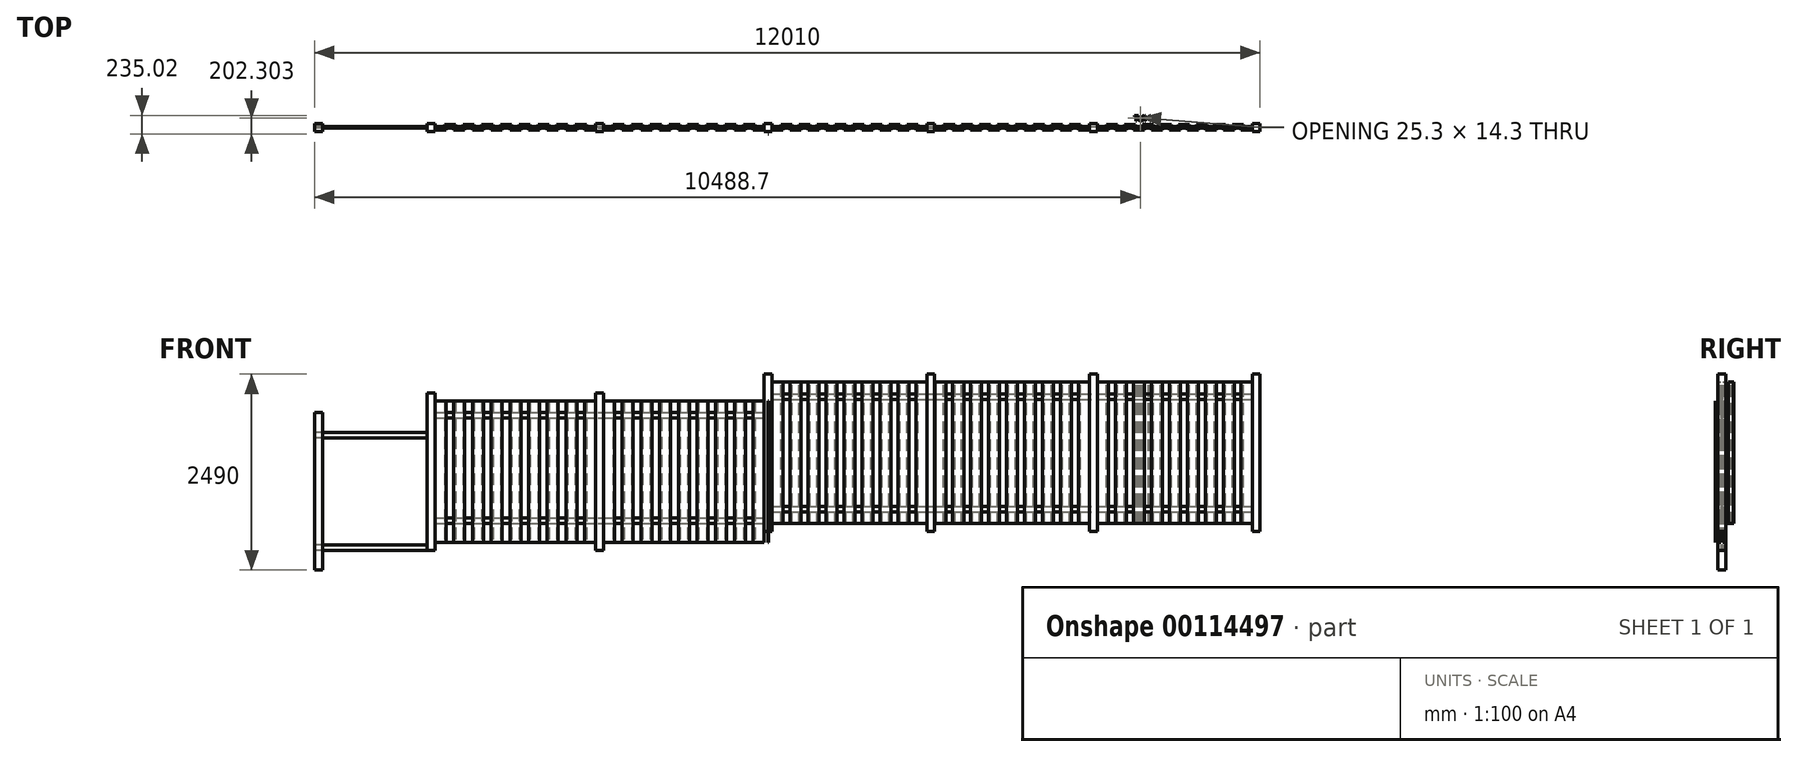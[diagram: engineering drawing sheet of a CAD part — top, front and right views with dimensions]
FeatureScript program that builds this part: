
annotation { "Feature Type Name" : "Feature", "Feature Type Description" : "" }
export const myFeature = defineFeature(function(context is Context, id is Id, definition is map)
    precondition{}
    {
        {
            var Q0;
            Q0=qCreatedBy(makeId("Top.planeOp"),FACE);
            var sketch = newSketch(context, id + "F0", { "sketchPlane" : qUnion([Q0])});
            skLineSegment(sketch, "E0.bottom", {"start": v(0, 0) * mm, "end": v(-100, 0) * mm});
            skLineSegment(sketch, "E0.top", {"start": v(0, 100) * mm, "end": v(-100, 100) * mm});
            skLineSegment(sketch, "E0.left", {"start": v(0, 0) * mm, "end": v(0, 100) * mm});
            skLineSegment(sketch, "E0.right", {"start": v(-100, 0) * mm, "end": v(-100, 100) * mm});
            skLineSegment(sketch, "E1.bottom", {"start": v(-6200, 0) * mm, "end": v(-6300, 0) * mm});
            skLineSegment(sketch, "E1.top", {"start": v(-6200, 100) * mm, "end": v(-6300, 100) * mm});
            skLineSegment(sketch, "E1.left", {"start": v(-6200, 0) * mm, "end": v(-6200, 100) * mm});
            skLineSegment(sketch, "E1.right", {"start": v(-6300, 0) * mm, "end": v(-6300, 100) * mm});
            skLineSegment(sketch, "E2.bottom", {"start": v(-10480, 0) * mm, "end": v(-10580, 0) * mm});
            skLineSegment(sketch, "E2.top", {"start": v(-10480, 100) * mm, "end": v(-10580, 100) * mm});
            skLineSegment(sketch, "E2.left", {"start": v(-10480, 0) * mm, "end": v(-10480, 100) * mm});
            skLineSegment(sketch, "E2.right", {"start": v(-10580, 0) * mm, "end": v(-10580, 100) * mm});
            skLineSegment(sketch, "E3.bottom", {"start": v(-2066.5, 0) * mm, "end": v(-2166.5, 0) * mm});
            skLineSegment(sketch, "E3.top", {"start": v(-2066.5, 100) * mm, "end": v(-2166.5, 100) * mm});
            skLineSegment(sketch, "E3.left", {"start": v(-2066.5, 0) * mm, "end": v(-2066.5, 100) * mm});
            skLineSegment(sketch, "E3.right", {"start": v(-2166.5, 0) * mm, "end": v(-2166.5, 100) * mm});
            skLineSegment(sketch, "E4.bottom", {"start": v(-4133, 0) * mm, "end": v(-4233, 0) * mm});
            skLineSegment(sketch, "E4.top", {"start": v(-4133, 100) * mm, "end": v(-4233, 100) * mm});
            skLineSegment(sketch, "E4.left", {"start": v(-4133, 0) * mm, "end": v(-4133, 100) * mm});
            skLineSegment(sketch, "E4.right", {"start": v(-4233, 0) * mm, "end": v(-4233, 100) * mm});
            skLineSegment(sketch, "E5.bottom", {"start": v(-11910, 0) * mm, "end": v(-12010, 0) * mm});
            skLineSegment(sketch, "E5.top", {"start": v(-11910, 100) * mm, "end": v(-12010, 100) * mm});
            skLineSegment(sketch, "E5.left", {"start": v(-11910, 0) * mm, "end": v(-11910, 100) * mm});
            skLineSegment(sketch, "E5.right", {"start": v(-12010, 0) * mm, "end": v(-12010, 100) * mm});
            skLineSegment(sketch, "E6.bottom", {"start": v(-8340, 0) * mm, "end": v(-8440, 0) * mm});
            skLineSegment(sketch, "E6.top", {"start": v(-8340, 100) * mm, "end": v(-8440, 100) * mm});
            skLineSegment(sketch, "E6.left", {"start": v(-8340, 0) * mm, "end": v(-8340, 100) * mm});
            skLineSegment(sketch, "E6.right", {"start": v(-8440, 0) * mm, "end": v(-8440, 100) * mm});
            skSolve(sketch);
        }
        {
            var Q0;
            Q0=makeQuery(id+"F0.imprint","IMPRINT",FACE,{"disambiguationData":[TD([[makeQuery(id+"F0.imprint","IMPRINT",EDGE,{"derivedFrom":sQuery(id+"F0.wireOp",EDGE,"E1.bottom")}),-1.0]])]});
            var Q1;
            Q1=makeQuery(id+"F0.imprint","IMPRINT",FACE,{"disambiguationData":[TD([[makeQuery(id+"F0.imprint","IMPRINT",EDGE,{"derivedFrom":sQuery(id+"F0.wireOp",EDGE,"E4.bottom")}),-1.0]])]});
            var Q2;
            Q2=makeQuery(id+"F0.imprint","IMPRINT",FACE,{"disambiguationData":[TD([[makeQuery(id+"F0.imprint","IMPRINT",EDGE,{"derivedFrom":sQuery(id+"F0.wireOp",EDGE,"E3.bottom")}),-1.0]])]});
            var Q3;
            Q3=makeQuery(id+"F0.imprint","IMPRINT",FACE,{"disambiguationData":[TD([[makeQuery(id+"F0.imprint","IMPRINT",EDGE,{"derivedFrom":sQuery(id+"F0.wireOp",EDGE,"E0.bottom")}),-1.0]])]});
            extrude(context, id + "F1", {"entities" : qUnion([Q0, Q1, Q2, Q3]), "depth" : 2000 * mm});
        }
        {
            var Q0;
            Q0=makeQuery(id+"F0.imprint","IMPRINT",FACE,{"disambiguationData":[TD([[makeQuery(id+"F0.imprint","IMPRINT",EDGE,{"derivedFrom":sQuery(id+"F0.wireOp",EDGE,"E6.bottom")}),-1.0]])]});
            var Q1;
            Q1=makeQuery(id+"F0.imprint","IMPRINT",FACE,{"disambiguationData":[TD([[makeQuery(id+"F0.imprint","IMPRINT",EDGE,{"derivedFrom":sQuery(id+"F0.wireOp",EDGE,"E2.bottom")}),-1.0]])]});
            extrude(context, id + "F2", {"entities" : qUnion([Q0, Q1]), "depth" : (2000 - 240) * mm, "hasSecondDirection" : true, "secondDirectionOppositeDirection" : true, "secondDirectionDepth" : 240 * mm});
        }
        {
            var Q0;
            Q0=makeQuery(id+"F0.imprint","IMPRINT",FACE,{"disambiguationData":[TD([[makeQuery(id+"F0.imprint","IMPRINT",EDGE,{"derivedFrom":sQuery(id+"F0.wireOp",EDGE,"E5.bottom")}),-1.0]])]});
            extrude(context, id + "F3", {"entities" : qUnion([Q0]), "depth" : (2000 - 490) * mm, "hasSecondDirection" : true, "secondDirectionOppositeDirection" : true, "secondDirectionDepth" : (240 + 250) * mm});
        }
        {
            var Q0;
            Q0=makeQuery(id+"F1.opExtrude","SWEPT_FACE",FACE,{"disambiguationData":[OSD([sQuery(id+"F0.wireOp",EDGE,"E0.left")])]});
            var sketch = newSketch(context, id + "F4", { "sketchPlane" : qUnion([Q0])});
            skLineSegment(sketch, "E7.bottom", {"start": v(39, 320) * mm, "end": v(61, 320) * mm});
            skLineSegment(sketch, "E7.top", {"start": v(39, 250) * mm, "end": v(61, 250) * mm});
            skLineSegment(sketch, "E7.left", {"start": v(39, 320) * mm, "end": v(39, 250) * mm});
            skLineSegment(sketch, "E7.right", {"start": v(61, 320) * mm, "end": v(61, 250) * mm});
            skLineSegment(sketch, "E8.bottom", {"start": v(39, 1680) * mm, "end": v(61, 1680) * mm});
            skLineSegment(sketch, "E8.top", {"start": v(39, 1750) * mm, "end": v(61, 1750) * mm});
            skLineSegment(sketch, "E8.left", {"start": v(39, 1680) * mm, "end": v(39, 1750) * mm});
            skLineSegment(sketch, "E8.right", {"start": v(61, 1680) * mm, "end": v(61, 1750) * mm});
            skSolve(sketch);
        }
        {
            var Q0;
            Q0 = qSketchRegion(id + "F4", true);
            var Q1;
            Q1=makeQuery(id+"F1.opExtrude","SWEPT_FACE",FACE,{"disambiguationData":[OSD([sQuery(id+"F0.wireOp",EDGE,"E1.left")])]});
            extrude(context, id + "F5", {"entities" : qUnion([Q0]), "endBound" : BoundingType.UP_TO_SURFACE, "oppositeDirection" : true, "endBoundEntityFace" : qUnion([Q1]), "depth" : 25 * mm, "hasSecondDirection" : true, "secondDirectionOppositeDirection" : true, "secondDirectionDepth" : 100 * mm});
        }
        {
            var Q0;
            Q0=makeQuery(id+"F1.opExtrude","SWEPT_FACE",FACE,{"disambiguationData":[OSD([sQuery(id+"F0.wireOp",EDGE,"E1.right")])]});
            var sketch = newSketch(context, id + "F6", { "sketchPlane" : qUnion([Q0])});
            skLineSegment(sketch, "E9.bottom", {"start": v(-39, 1510) * mm, "end": v(-61, 1510) * mm});
            skLineSegment(sketch, "E9.top", {"start": v(-39, 1440) * mm, "end": v(-61, 1440) * mm});
            skLineSegment(sketch, "E9.left", {"start": v(-39, 1510) * mm, "end": v(-39, 1440) * mm});
            skLineSegment(sketch, "E9.right", {"start": v(-61, 1510) * mm, "end": v(-61, 1440) * mm});
            skLineSegment(sketch, "E10.bottom", {"start": v(-39, 174.78) * mm, "end": v(-61, 174.78) * mm});
            skLineSegment(sketch, "E10.top", {"start": v(-39, 104.78) * mm, "end": v(-61, 104.78) * mm});
            skLineSegment(sketch, "E10.left", {"start": v(-39, 174.78) * mm, "end": v(-39, 104.78) * mm});
            skLineSegment(sketch, "E10.right", {"start": v(-61, 174.78) * mm, "end": v(-61, 104.78) * mm});
            skSolve(sketch);
        }
        {
            var Q0;
            Q0 = qSketchRegion(id + "F6", true);
            var Q1;
            Q1=makeQuery(id+"F2.opExtrude","SWEPT_FACE",FACE,{"disambiguationData":[OSD([sQuery(id+"F0.wireOp",EDGE,"E2.left")])]});
            extrude(context, id + "F7", {"entities" : qUnion([Q0]), "endBound" : BoundingType.UP_TO_SURFACE, "endBoundEntityFace" : qUnion([Q1]), "depth" : 25 * mm});
        }
        {
            var Q0;
            Q0=makeQuery(id+"F1.opExtrude","CAP_FACE",FACE,{"disambiguationData":[OSD([sQuery(id+"F0.wireOp",EDGE,"E3.bottom"),sQuery(id+"F0.wireOp",EDGE,"E3.top"),sQuery(id+"F0.wireOp",EDGE,"E3.left"),sQuery(id+"F0.wireOp",EDGE,"E3.right")])],"isStart":false});
            var sketch = newSketch(context, id + "F8", { "sketchPlane" : qUnion([Q0])});
            skLineSegment(sketch, "E11.bottom", {"start": v(-2066.5, 39) * mm, "end": v(-1926.5, 39) * mm});
            skLineSegment(sketch, "E11.top", {"start": v(-2066.5, 17) * mm, "end": v(-1926.5, 17) * mm});
            skLineSegment(sketch, "E11.left", {"start": v(-2066.5, 39) * mm, "end": v(-2066.5, 17) * mm});
            skLineSegment(sketch, "E11.right", {"start": v(-1926.5, 39) * mm, "end": v(-1926.5, 17) * mm});
            skLineSegment(sketch, "E12.1.0.0", {"start": v(-1838.2, 39) * mm, "end": v(-1838.2, 17) * mm});
            skLineSegment(sketch, "E12.1.0.1", {"start": v(-1838.2, 17) * mm, "end": v(-1698.2, 17) * mm});
            skLineSegment(sketch, "E12.1.0.2", {"start": v(-1838.2, 39) * mm, "end": v(-1698.2, 39) * mm});
            skLineSegment(sketch, "E12.1.0.3", {"start": v(-1698.2, 39) * mm, "end": v(-1698.2, 17) * mm});
            skLineSegment(sketch, "E12.2.0.0", {"start": v(-1609.9, 39) * mm, "end": v(-1609.9, 17) * mm});
            skLineSegment(sketch, "E12.2.0.1", {"start": v(-1609.9, 17) * mm, "end": v(-1469.9, 17) * mm});
            skLineSegment(sketch, "E12.2.0.2", {"start": v(-1609.9, 39) * mm, "end": v(-1469.9, 39) * mm});
            skLineSegment(sketch, "E12.2.0.3", {"start": v(-1469.9, 39) * mm, "end": v(-1469.9, 17) * mm});
            skLineSegment(sketch, "E12.3.0.0", {"start": v(-1381.6, 39) * mm, "end": v(-1381.6, 17) * mm});
            skLineSegment(sketch, "E12.3.0.1", {"start": v(-1381.6, 17) * mm, "end": v(-1241.6, 17) * mm});
            skLineSegment(sketch, "E12.3.0.2", {"start": v(-1381.6, 39) * mm, "end": v(-1241.6, 39) * mm});
            skLineSegment(sketch, "E12.3.0.3", {"start": v(-1241.6, 39) * mm, "end": v(-1241.6, 17) * mm});
            skLineSegment(sketch, "E12.4.0.0", {"start": v(-1153.3, 39) * mm, "end": v(-1153.3, 17) * mm});
            skLineSegment(sketch, "E12.4.0.1", {"start": v(-1153.3, 17) * mm, "end": v(-1013.3, 17) * mm});
            skLineSegment(sketch, "E12.4.0.2", {"start": v(-1153.3, 39) * mm, "end": v(-1013.3, 39) * mm});
            skLineSegment(sketch, "E12.4.0.3", {"start": v(-1013.3, 39) * mm, "end": v(-1013.3, 17) * mm});
            skLineSegment(sketch, "E12.5.0.0", {"start": v(-925, 39) * mm, "end": v(-925, 17) * mm});
            skLineSegment(sketch, "E12.5.0.1", {"start": v(-925, 17) * mm, "end": v(-785, 17) * mm});
            skLineSegment(sketch, "E12.5.0.2", {"start": v(-925, 39) * mm, "end": v(-785, 39) * mm});
            skLineSegment(sketch, "E12.5.0.3", {"start": v(-785, 39) * mm, "end": v(-785, 17) * mm});
            skLineSegment(sketch, "E12.6.0.0", {"start": v(-696.7, 39) * mm, "end": v(-696.7, 17) * mm});
            skLineSegment(sketch, "E12.6.0.1", {"start": v(-696.7, 17) * mm, "end": v(-556.7, 17) * mm});
            skLineSegment(sketch, "E12.6.0.2", {"start": v(-696.7, 39) * mm, "end": v(-556.7, 39) * mm});
            skLineSegment(sketch, "E12.6.0.3", {"start": v(-556.7, 39) * mm, "end": v(-556.7, 17) * mm});
            skLineSegment(sketch, "E12.7.0.0", {"start": v(-468.4, 39) * mm, "end": v(-468.4, 17) * mm});
            skLineSegment(sketch, "E12.7.0.1", {"start": v(-468.4, 17) * mm, "end": v(-328.4, 17) * mm});
            skLineSegment(sketch, "E12.7.0.2", {"start": v(-468.4, 39) * mm, "end": v(-328.4, 39) * mm});
            skLineSegment(sketch, "E12.7.0.3", {"start": v(-328.4, 39) * mm, "end": v(-328.4, 17) * mm});
            skLineSegment(sketch, "E12.8.0.0", {"start": v(-240.1, 39) * mm, "end": v(-240.1, 17) * mm});
            skLineSegment(sketch, "E12.8.0.1", {"start": v(-240.1, 17) * mm, "end": v(-100.1, 17) * mm});
            skLineSegment(sketch, "E12.8.0.2", {"start": v(-240.1, 39) * mm, "end": v(-100.1, 39) * mm});
            skLineSegment(sketch, "E12.8.0.3", {"start": v(-100.1, 39) * mm, "end": v(-100.1, 17) * mm});
            skLineSegment(sketch, "E12.direction1", {"start": v(-2066.5, 17) * mm, "end": v(-1838.2, 17) * mm, "construction": true});
            skLineSegment(sketch, "E13.bottom", {"start": v(-1952.35, 61) * mm, "end": v(-1812.35, 61) * mm});
            skLineSegment(sketch, "E13.top", {"start": v(-1952.35, 83) * mm, "end": v(-1812.35, 83) * mm});
            skLineSegment(sketch, "E13.left", {"start": v(-1952.35, 61) * mm, "end": v(-1952.35, 83) * mm});
            skLineSegment(sketch, "E13.right", {"start": v(-1812.35, 61) * mm, "end": v(-1812.35, 83) * mm});
            skLineSegment(sketch, "E14", {"start": v(-1882.35, -3.63) * mm, "end": v(-1882.35, 53.31) * mm, "construction": true});
            skLineSegment(sketch, "E15.1.0.0", {"start": v(-1584.05, 61) * mm, "end": v(-1584.05, 83) * mm});
            skLineSegment(sketch, "E15.1.0.1", {"start": v(-1724.05, 83) * mm, "end": v(-1584.05, 83) * mm});
            skLineSegment(sketch, "E15.1.0.2", {"start": v(-1724.05, 61) * mm, "end": v(-1724.05, 83) * mm});
            skLineSegment(sketch, "E15.1.0.3", {"start": v(-1724.05, 61) * mm, "end": v(-1584.05, 61) * mm});
            skLineSegment(sketch, "E15.2.0.0", {"start": v(-1355.75, 61) * mm, "end": v(-1355.75, 83) * mm});
            skLineSegment(sketch, "E15.2.0.1", {"start": v(-1495.75, 83) * mm, "end": v(-1355.75, 83) * mm});
            skLineSegment(sketch, "E15.2.0.2", {"start": v(-1495.75, 61) * mm, "end": v(-1495.75, 83) * mm});
            skLineSegment(sketch, "E15.2.0.3", {"start": v(-1495.75, 61) * mm, "end": v(-1355.75, 61) * mm});
            skLineSegment(sketch, "E15.3.0.0", {"start": v(-1127.45, 61) * mm, "end": v(-1127.45, 83) * mm});
            skLineSegment(sketch, "E15.3.0.1", {"start": v(-1267.45, 83) * mm, "end": v(-1127.45, 83) * mm});
            skLineSegment(sketch, "E15.3.0.2", {"start": v(-1267.45, 61) * mm, "end": v(-1267.45, 83) * mm});
            skLineSegment(sketch, "E15.3.0.3", {"start": v(-1267.45, 61) * mm, "end": v(-1127.45, 61) * mm});
            skLineSegment(sketch, "E15.4.0.0", {"start": v(-899.15, 61) * mm, "end": v(-899.15, 83) * mm});
            skLineSegment(sketch, "E15.4.0.1", {"start": v(-1039.15, 83) * mm, "end": v(-899.15, 83) * mm});
            skLineSegment(sketch, "E15.4.0.2", {"start": v(-1039.15, 61) * mm, "end": v(-1039.15, 83) * mm});
            skLineSegment(sketch, "E15.4.0.3", {"start": v(-1039.15, 61) * mm, "end": v(-899.15, 61) * mm});
            skLineSegment(sketch, "E15.5.0.0", {"start": v(-670.85, 61) * mm, "end": v(-670.85, 83) * mm});
            skLineSegment(sketch, "E15.5.0.1", {"start": v(-810.85, 83) * mm, "end": v(-670.85, 83) * mm});
            skLineSegment(sketch, "E15.5.0.2", {"start": v(-810.85, 61) * mm, "end": v(-810.85, 83) * mm});
            skLineSegment(sketch, "E15.5.0.3", {"start": v(-810.85, 61) * mm, "end": v(-670.85, 61) * mm});
            skLineSegment(sketch, "E15.6.0.0", {"start": v(-442.55, 61) * mm, "end": v(-442.55, 83) * mm});
            skLineSegment(sketch, "E15.6.0.1", {"start": v(-582.55, 83) * mm, "end": v(-442.55, 83) * mm});
            skLineSegment(sketch, "E15.6.0.2", {"start": v(-582.55, 61) * mm, "end": v(-582.55, 83) * mm});
            skLineSegment(sketch, "E15.6.0.3", {"start": v(-582.55, 61) * mm, "end": v(-442.55, 61) * mm});
            skLineSegment(sketch, "E15.7.0.0", {"start": v(-214.25, 61) * mm, "end": v(-214.25, 83) * mm});
            skLineSegment(sketch, "E15.7.0.1", {"start": v(-354.25, 83) * mm, "end": v(-214.25, 83) * mm});
            skLineSegment(sketch, "E15.7.0.2", {"start": v(-354.25, 61) * mm, "end": v(-354.25, 83) * mm});
            skLineSegment(sketch, "E15.7.0.3", {"start": v(-354.25, 61) * mm, "end": v(-214.25, 61) * mm});
            skLineSegment(sketch, "E15.direction1", {"start": v(-1952.35, 61) * mm, "end": v(-1724.05, 61) * mm, "construction": true});
            skLineSegment(sketch, "E16", {"start": v(-2116.5, 100) * mm, "end": v(-2116.5, 142.57) * mm, "construction": true});
            skLineSegment(sketch, "E17.MirrorCS", {"start": v(-2394.8, 39) * mm, "end": v(-2394.8, 17) * mm});
            skLineSegment(sketch, "E18.MirrorCS", {"start": v(-2166.5, 39) * mm, "end": v(-2166.5, 17) * mm});
            skLineSegment(sketch, "E19.MirrorCS", {"start": v(-2508.95, 61) * mm, "end": v(-2508.95, 83) * mm});
            skLineSegment(sketch, "E20.MirrorCS", {"start": v(-2280.65, 61) * mm, "end": v(-2280.65, 83) * mm});
            skLineSegment(sketch, "E21.MirrorCS", {"start": v(-2534.8, 39) * mm, "end": v(-2534.8, 17) * mm});
            skLineSegment(sketch, "E22.MirrorCS", {"start": v(-2306.5, 39) * mm, "end": v(-2306.5, 17) * mm});
            skLineSegment(sketch, "E23.MirrorCS", {"start": v(-2991.4, 39) * mm, "end": v(-2991.4, 17) * mm});
            skLineSegment(sketch, "E24.MirrorCS", {"start": v(-3333.85, 61) * mm, "end": v(-3333.85, 83) * mm});
            skLineSegment(sketch, "E25.MirrorCS", {"start": v(-3904.6, 39) * mm, "end": v(-3904.6, 17) * mm});
            skLineSegment(sketch, "E26.MirrorCS", {"start": v(-2877.25, 61) * mm, "end": v(-2877.25, 83) * mm});
            skLineSegment(sketch, "E27.MirrorCS", {"start": v(-3790.45, 61) * mm, "end": v(-3790.45, 83) * mm});
            skLineSegment(sketch, "E28.MirrorCS", {"start": v(-3764.6, 39) * mm, "end": v(-3764.6, 17) * mm});
            skLineSegment(sketch, "E29.MirrorCS", {"start": v(-3422.15, 61) * mm, "end": v(-3422.15, 83) * mm});
            skLineSegment(sketch, "E30.MirrorCS", {"start": v(-2965.55, 61) * mm, "end": v(-2965.55, 83) * mm});
            skLineSegment(sketch, "E31.MirrorCS", {"start": v(-3878.75, 61) * mm, "end": v(-3878.75, 83) * mm});
            skLineSegment(sketch, "E32.MirrorCS", {"start": v(-3308, 39) * mm, "end": v(-3308, 17) * mm});
            skLineSegment(sketch, "E33.MirrorCS", {"start": v(-3992.9, 39) * mm, "end": v(-3992.9, 17) * mm});
            skLineSegment(sketch, "E34.MirrorCS", {"start": v(-3676.3, 39) * mm, "end": v(-3676.3, 17) * mm});
            skLineSegment(sketch, "E35.MirrorCS", {"start": v(-3562.15, 61) * mm, "end": v(-3562.15, 83) * mm});
            skLineSegment(sketch, "E36.MirrorCS", {"start": v(-2648.95, 61) * mm, "end": v(-2648.95, 83) * mm});
            skLineSegment(sketch, "E37.MirrorCS", {"start": v(-3448, 39) * mm, "end": v(-3448, 17) * mm});
            skLineSegment(sketch, "E38.MirrorCS", {"start": v(-4132.9, 39) * mm, "end": v(-4132.9, 17) * mm});
            skLineSegment(sketch, "E39.MirrorCS", {"start": v(-3219.7, 39) * mm, "end": v(-3219.7, 17) * mm});
            skLineSegment(sketch, "E40.MirrorCS", {"start": v(-2623.1, 39) * mm, "end": v(-2623.1, 17) * mm});
            skLineSegment(sketch, "E41.MirrorCS", {"start": v(-3079.7, 39) * mm, "end": v(-3079.7, 17) * mm});
            skLineSegment(sketch, "E42.MirrorCS", {"start": v(-4018.75, 61) * mm, "end": v(-4018.75, 83) * mm});
            skLineSegment(sketch, "E43.MirrorCS", {"start": v(-3650.45, 61) * mm, "end": v(-3650.45, 83) * mm});
            skLineSegment(sketch, "E44.MirrorCS", {"start": v(-2737.25, 61) * mm, "end": v(-2737.25, 83) * mm});
            skLineSegment(sketch, "E45.MirrorCS", {"start": v(-2763.1, 39) * mm, "end": v(-2763.1, 17) * mm});
            skLineSegment(sketch, "E46.MirrorCS", {"start": v(-3536.3, 39) * mm, "end": v(-3536.3, 17) * mm});
            skLineSegment(sketch, "E47.MirrorCS", {"start": v(-2420.65, 61) * mm, "end": v(-2420.65, 83) * mm});
            skLineSegment(sketch, "E48.MirrorCS", {"start": v(-3193.85, 61) * mm, "end": v(-3193.85, 83) * mm});
            skLineSegment(sketch, "E49.MirrorCS", {"start": v(-3105.55, 61) * mm, "end": v(-3105.55, 83) * mm});
            skLineSegment(sketch, "E50.MirrorCS", {"start": v(-2851.4, 39) * mm, "end": v(-2851.4, 17) * mm});
            skLineSegment(sketch, "E51.MirrorCS", {"start": v(-2166.5, 17) * mm, "end": v(-2306.5, 17) * mm});
            skLineSegment(sketch, "E52.MirrorCS", {"start": v(-2280.65, 61) * mm, "end": v(-2420.65, 61) * mm});
            skLineSegment(sketch, "E53.MirrorCS", {"start": v(-2350.65, -3.63) * mm, "end": v(-2350.65, 53.31) * mm, "construction": true});
            skLineSegment(sketch, "E54.MirrorCS", {"start": v(-2394.8, 39) * mm, "end": v(-2534.8, 39) * mm});
            skLineSegment(sketch, "E55.MirrorCS", {"start": v(-2394.8, 17) * mm, "end": v(-2534.8, 17) * mm});
            skLineSegment(sketch, "E56.MirrorCS", {"start": v(-2166.5, 39) * mm, "end": v(-2306.5, 39) * mm});
            skLineSegment(sketch, "E57.MirrorCS", {"start": v(-2851.4, 39) * mm, "end": v(-2991.4, 39) * mm});
            skLineSegment(sketch, "E58.MirrorCS", {"start": v(-2851.4, 17) * mm, "end": v(-2991.4, 17) * mm});
            skLineSegment(sketch, "E59.MirrorCS", {"start": v(-2737.25, 83) * mm, "end": v(-2877.25, 83) * mm});
            skLineSegment(sketch, "E60.MirrorCS", {"start": v(-3650.45, 83) * mm, "end": v(-3790.45, 83) * mm});
            skLineSegment(sketch, "E61.MirrorCS", {"start": v(-2166.5, 17) * mm, "end": v(-2394.8, 17) * mm, "construction": true});
            skLineSegment(sketch, "E62.MirrorCS", {"start": v(-2280.65, 61) * mm, "end": v(-2508.95, 61) * mm, "construction": true});
            skLineSegment(sketch, "E63.MirrorCS", {"start": v(-3308, 39) * mm, "end": v(-3448, 39) * mm});
            skLineSegment(sketch, "E64.MirrorCS", {"start": v(-2280.65, 83) * mm, "end": v(-2420.65, 83) * mm});
            skLineSegment(sketch, "E65.MirrorCS", {"start": v(-2965.55, 61) * mm, "end": v(-3105.55, 61) * mm});
            skLineSegment(sketch, "E66.MirrorCS", {"start": v(-3878.75, 61) * mm, "end": v(-4018.75, 61) * mm});
            skLineSegment(sketch, "E67.MirrorCS", {"start": v(-3308, 17) * mm, "end": v(-3448, 17) * mm});
            skLineSegment(sketch, "E68.MirrorCS", {"start": v(-3764.6, 39) * mm, "end": v(-3904.6, 39) * mm});
            skLineSegment(sketch, "E69.MirrorCS", {"start": v(-2508.95, 61) * mm, "end": v(-2648.95, 61) * mm});
            skLineSegment(sketch, "E70.MirrorCS", {"start": v(-3422.15, 61) * mm, "end": v(-3562.15, 61) * mm});
            skLineSegment(sketch, "E71.MirrorCS", {"start": v(-3764.6, 17) * mm, "end": v(-3904.6, 17) * mm});
            skLineSegment(sketch, "E72.MirrorCS", {"start": v(-2623.1, 17) * mm, "end": v(-2763.1, 17) * mm});
            skLineSegment(sketch, "E73.MirrorCS", {"start": v(-2508.95, 83) * mm, "end": v(-2648.95, 83) * mm});
            skLineSegment(sketch, "E74.MirrorCS", {"start": v(-3536.3, 39) * mm, "end": v(-3676.3, 39) * mm});
            skLineSegment(sketch, "E75.MirrorCS", {"start": v(-3193.85, 83) * mm, "end": v(-3333.85, 83) * mm});
            skLineSegment(sketch, "E76.MirrorCS", {"start": v(-3992.9, 17) * mm, "end": v(-4132.9, 17) * mm});
            skLineSegment(sketch, "E77.MirrorCS", {"start": v(-3079.7, 17) * mm, "end": v(-3219.7, 17) * mm});
            skLineSegment(sketch, "E78.MirrorCS", {"start": v(-3650.45, 61) * mm, "end": v(-3790.45, 61) * mm});
            skLineSegment(sketch, "E79.MirrorCS", {"start": v(-2737.25, 61) * mm, "end": v(-2877.25, 61) * mm});
            skLineSegment(sketch, "E80.MirrorCS", {"start": v(-3878.75, 83) * mm, "end": v(-4018.75, 83) * mm});
            skLineSegment(sketch, "E81.MirrorCS", {"start": v(-2965.55, 83) * mm, "end": v(-3105.55, 83) * mm});
            skLineSegment(sketch, "E82.MirrorCS", {"start": v(-3422.15, 83) * mm, "end": v(-3562.15, 83) * mm});
            skLineSegment(sketch, "E83.MirrorCS", {"start": v(-2623.1, 39) * mm, "end": v(-2763.1, 39) * mm});
            skLineSegment(sketch, "E84.MirrorCS", {"start": v(-3536.3, 17) * mm, "end": v(-3676.3, 17) * mm});
            skLineSegment(sketch, "E85.MirrorCS", {"start": v(-3193.85, 61) * mm, "end": v(-3333.85, 61) * mm});
            skLineSegment(sketch, "E86.MirrorCS", {"start": v(-3992.9, 39) * mm, "end": v(-4132.9, 39) * mm});
            skLineSegment(sketch, "E87.MirrorCS", {"start": v(-3079.7, 39) * mm, "end": v(-3219.7, 39) * mm});
            skLineSegment(sketch, "E88", {"start": v(-4183, 101.05) * mm, "end": v(-4183, 169.36) * mm, "construction": true});
            skLineSegment(sketch, "E89.MirrorCS", {"start": v(-4233.1, 39) * mm, "end": v(-4233.1, 17) * mm});
            skLineSegment(sketch, "E90.MirrorCS", {"start": v(-6199.5, 39) * mm, "end": v(-6199.5, 17) * mm});
            skLineSegment(sketch, "E91.MirrorCS", {"start": v(-5286.3, 39) * mm, "end": v(-5286.3, 17) * mm});
            skLineSegment(sketch, "E92.MirrorCS", {"start": v(-4461.4, 39) * mm, "end": v(-4461.4, 17) * mm});
            skLineSegment(sketch, "E93.MirrorCS", {"start": v(-4347.25, 61) * mm, "end": v(-4347.25, 83) * mm});
            skLineSegment(sketch, "E94.MirrorCS", {"start": v(-5488.75, 61) * mm, "end": v(-5488.75, 83) * mm});
            skLineSegment(sketch, "E95.MirrorCS", {"start": v(-4575.55, 61) * mm, "end": v(-4575.55, 83) * mm});
            skLineSegment(sketch, "E96.MirrorCS", {"start": v(-5400.45, 61) * mm, "end": v(-5400.45, 83) * mm});
            skLineSegment(sketch, "E97.MirrorCS", {"start": v(-5945.35, 61) * mm, "end": v(-5945.35, 83) * mm});
            skLineSegment(sketch, "E98.MirrorCS", {"start": v(-5971.2, 39) * mm, "end": v(-5971.2, 17) * mm});
            skLineSegment(sketch, "E99.MirrorCS", {"start": v(-6199.5, 17) * mm, "end": v(-6059.5, 17) * mm});
            skLineSegment(sketch, "E100.MirrorCS", {"start": v(-5514.6, 39) * mm, "end": v(-5514.6, 17) * mm});
            skLineSegment(sketch, "E101.MirrorCS", {"start": v(-5857.05, 83) * mm, "end": v(-5717.05, 83) * mm});
            skLineSegment(sketch, "E102.MirrorCS", {"start": v(-5514.6, 39) * mm, "end": v(-5374.6, 39) * mm});
            skLineSegment(sketch, "E103.MirrorCS", {"start": v(-4829.7, 39) * mm, "end": v(-4689.7, 39) * mm});
            skLineSegment(sketch, "E104.MirrorCS", {"start": v(-5514.6, 17) * mm, "end": v(-5374.6, 17) * mm});
            skLineSegment(sketch, "E105.MirrorCS", {"start": v(-4715.55, 61) * mm, "end": v(-4715.55, 83) * mm});
            skLineSegment(sketch, "E106.MirrorCS", {"start": v(-5172.15, 83) * mm, "end": v(-5032.15, 83) * mm});
            skLineSegment(sketch, "E107.MirrorCS", {"start": v(-5628.75, 83) * mm, "end": v(-5488.75, 83) * mm});
            skLineSegment(sketch, "E108.MirrorCS", {"start": v(-4715.55, 83) * mm, "end": v(-4575.55, 83) * mm});
            skLineSegment(sketch, "E109.MirrorCS", {"start": v(-5628.75, 61) * mm, "end": v(-5628.75, 83) * mm});
            skLineSegment(sketch, "E110.MirrorCS", {"start": v(-4601.4, 39) * mm, "end": v(-4601.4, 17) * mm});
            skLineSegment(sketch, "E111.MirrorCS", {"start": v(-5602.9, 39) * mm, "end": v(-5602.9, 17) * mm});
            skLineSegment(sketch, "E112.MirrorCS", {"start": v(-5286.3, 17) * mm, "end": v(-5146.3, 17) * mm});
            skLineSegment(sketch, "E113.MirrorCS", {"start": v(-6199.5, 17) * mm, "end": v(-5971.2, 17) * mm, "construction": true});
            skLineSegment(sketch, "E114.MirrorCS", {"start": v(-4829.7, 39) * mm, "end": v(-4829.7, 17) * mm});
            skLineSegment(sketch, "E115.MirrorCS", {"start": v(-4715.55, 61) * mm, "end": v(-4575.55, 61) * mm});
            skLineSegment(sketch, "E116.MirrorCS", {"start": v(-6085.35, 61) * mm, "end": v(-5857.05, 61) * mm, "construction": true});
            skLineSegment(sketch, "E117.MirrorCS", {"start": v(-4487.25, 61) * mm, "end": v(-4487.25, 83) * mm});
            skLineSegment(sketch, "E118.MirrorCS", {"start": v(-5628.75, 61) * mm, "end": v(-5488.75, 61) * mm});
            skLineSegment(sketch, "E119.MirrorCS", {"start": v(-4487.25, 83) * mm, "end": v(-4347.25, 83) * mm});
            skLineSegment(sketch, "E120.MirrorCS", {"start": v(-6199.5, 39) * mm, "end": v(-6059.5, 39) * mm});
            skLineSegment(sketch, "E121.MirrorCS", {"start": v(-5742.9, 17) * mm, "end": v(-5602.9, 17) * mm});
            skLineSegment(sketch, "E122.MirrorCS", {"start": v(-5717.05, 61) * mm, "end": v(-5717.05, 83) * mm});
            skLineSegment(sketch, "E123.MirrorCS", {"start": v(-6085.35, 61) * mm, "end": v(-5945.35, 61) * mm});
            skLineSegment(sketch, "E124.MirrorCS", {"start": v(-4601.4, 39) * mm, "end": v(-4461.4, 39) * mm});
            skLineSegment(sketch, "E125.MirrorCS", {"start": v(-4829.7, 17) * mm, "end": v(-4689.7, 17) * mm});
            skLineSegment(sketch, "E126.MirrorCS", {"start": v(-5742.9, 39) * mm, "end": v(-5742.9, 17) * mm});
            skLineSegment(sketch, "E127.MirrorCS", {"start": v(-5032.15, 61) * mm, "end": v(-5032.15, 83) * mm});
            skLineSegment(sketch, "E128.MirrorCS", {"start": v(-6085.35, 61) * mm, "end": v(-6085.35, 83) * mm});
            skLineSegment(sketch, "E129.MirrorCS", {"start": v(-5971.2, 17) * mm, "end": v(-5831.2, 17) * mm});
            skLineSegment(sketch, "E130.MirrorCS", {"start": v(-4601.4, 17) * mm, "end": v(-4461.4, 17) * mm});
            skLineSegment(sketch, "E131.MirrorCS", {"start": v(-5286.3, 39) * mm, "end": v(-5146.3, 39) * mm});
            skLineSegment(sketch, "E132.MirrorCS", {"start": v(-5374.6, 39) * mm, "end": v(-5374.6, 17) * mm});
            skLineSegment(sketch, "E133.MirrorCS", {"start": v(-5146.3, 39) * mm, "end": v(-5146.3, 17) * mm});
            skLineSegment(sketch, "E134.MirrorCS", {"start": v(-5400.45, 83) * mm, "end": v(-5260.45, 83) * mm});
            skLineSegment(sketch, "E135.MirrorCS", {"start": v(-5260.45, 61) * mm, "end": v(-5260.45, 83) * mm});
            skLineSegment(sketch, "E136.MirrorCS", {"start": v(-6059.5, 39) * mm, "end": v(-6059.5, 17) * mm});
            skLineSegment(sketch, "E137.MirrorCS", {"start": v(-5831.2, 39) * mm, "end": v(-5831.2, 17) * mm});
            skLineSegment(sketch, "E138.MirrorCS", {"start": v(-5857.05, 61) * mm, "end": v(-5857.05, 83) * mm});
            skLineSegment(sketch, "E139.MirrorCS", {"start": v(-5172.15, 61) * mm, "end": v(-5032.15, 61) * mm});
            skLineSegment(sketch, "E140.MirrorCS", {"start": v(-5742.9, 39) * mm, "end": v(-5602.9, 39) * mm});
            skLineSegment(sketch, "E141.MirrorCS", {"start": v(-5857.05, 61) * mm, "end": v(-5717.05, 61) * mm});
            skLineSegment(sketch, "E142.MirrorCS", {"start": v(-6015.35, -3.63) * mm, "end": v(-6015.35, 53.31) * mm, "construction": true});
            skLineSegment(sketch, "E143.MirrorCS", {"start": v(-4803.85, 61) * mm, "end": v(-4803.85, 83) * mm});
            skLineSegment(sketch, "E144.MirrorCS", {"start": v(-5058, 39) * mm, "end": v(-5058, 17) * mm});
            skLineSegment(sketch, "E145.MirrorCS", {"start": v(-5172.15, 61) * mm, "end": v(-5172.15, 83) * mm});
            skLineSegment(sketch, "E146.MirrorCS", {"start": v(-4373.1, 39) * mm, "end": v(-4373.1, 17) * mm});
            skLineSegment(sketch, "E147.MirrorCS", {"start": v(-6085.35, 83) * mm, "end": v(-5945.35, 83) * mm});
            skLineSegment(sketch, "E148.MirrorCS", {"start": v(-5400.45, 61) * mm, "end": v(-5260.45, 61) * mm});
            skLineSegment(sketch, "E149.MirrorCS", {"start": v(-5971.2, 39) * mm, "end": v(-5831.2, 39) * mm});
            skLineSegment(sketch, "E150.MirrorCS", {"start": v(-4487.25, 61) * mm, "end": v(-4347.25, 61) * mm});
            skLineSegment(sketch, "E151.MirrorCS", {"start": v(-4689.7, 39) * mm, "end": v(-4689.7, 17) * mm});
            skLineSegment(sketch, "E152.MirrorCS", {"start": v(-4373.1, 17) * mm, "end": v(-4233.1, 17) * mm});
            skLineSegment(sketch, "E153.MirrorCS", {"start": v(-4943.85, 61) * mm, "end": v(-4943.85, 83) * mm});
            skLineSegment(sketch, "E154.MirrorCS", {"start": v(-5058, 39) * mm, "end": v(-4918, 39) * mm});
            skLineSegment(sketch, "E155.MirrorCS", {"start": v(-5058, 17) * mm, "end": v(-4918, 17) * mm});
            skLineSegment(sketch, "E156.MirrorCS", {"start": v(-4918, 39) * mm, "end": v(-4918, 17) * mm});
            skLineSegment(sketch, "E157.MirrorCS", {"start": v(-4943.85, 61) * mm, "end": v(-4803.85, 61) * mm});
            skLineSegment(sketch, "E158.MirrorCS", {"start": v(-4373.1, 39) * mm, "end": v(-4233.1, 39) * mm});
            skLineSegment(sketch, "E159.MirrorCS", {"start": v(-4943.85, 83) * mm, "end": v(-4803.85, 83) * mm});
            skLineSegment(sketch, "E160", {"start": v(-1882.35, 83) * mm, "end": v(-1882.35, 141.03) * mm, "construction": true});
            skLineSegment(sketch, "E161", {"start": v(-1654.05, 83) * mm, "end": v(-1654.05, 136.93) * mm, "construction": true});
            skLineSegment(sketch, "E162", {"start": v(-1768.2, 17) * mm, "end": v(-1768.2, -41.18) * mm, "construction": true});
            skText(sketch, "E163", { "text": "Teil 1\n", "fontName": "OpenSans-Regular.ttf"});
            const initialGuessF8  = {"E163": [-1.5968, 0.13263, 1, 0, 0.0651]};
            skSetInitialGuess(sketch, initialGuessF8);
            skSolve(sketch);
        }
        {
            var Q0;
            Q0 = qSketchRegion(id + "F8", true);
            extrude(context, id + "F9", {"entities" : qUnion([Q0]), "oppositeDirection" : true, "depth" : 1900 * mm, "hasSecondDirection" : true, "secondDirectionOppositeDirection" : true, "secondDirectionDepth" : 100 * mm});
        }
        {
            var Q0;
            Q0=makeQuery(id+"F2.opExtrude","CAP_FACE",FACE,{"disambiguationData":[OSD([sQuery(id+"F0.wireOp",EDGE,"E6.bottom"),sQuery(id+"F0.wireOp",EDGE,"E6.top"),sQuery(id+"F0.wireOp",EDGE,"E6.left"),sQuery(id+"F0.wireOp",EDGE,"E6.right")])],"isStart":true});
            var sketch = newSketch(context, id + "F10", { "sketchPlane" : qUnion([Q0])});
            skLineSegment(sketch, "E164.bottom", {"start": v(-6300, -39) * mm, "end": v(-6440, -39) * mm});
            skLineSegment(sketch, "E164.top", {"start": v(-6300, -17) * mm, "end": v(-6440, -17) * mm});
            skLineSegment(sketch, "E164.left", {"start": v(-6300, -39) * mm, "end": v(-6300, -17) * mm});
            skLineSegment(sketch, "E164.right", {"start": v(-6440, -39) * mm, "end": v(-6440, -17) * mm});
            skLineSegment(sketch, "E165.bottom", {"start": v(-6248.22, 33.2) * mm, "end": v(-6245.72, 33.2) * mm});
            skLineSegment(sketch, "E165.top", {"start": v(-6248.22, 33.7) * mm, "end": v(-6245.72, 33.7) * mm});
            skLineSegment(sketch, "E165.left", {"start": v(-6248.22, 33.2) * mm, "end": v(-6248.22, 33.7) * mm});
            skLineSegment(sketch, "E165.right", {"start": v(-6245.72, 33.2) * mm, "end": v(-6245.72, 33.7) * mm});
            skLineSegment(sketch, "E166.1.0.0", {"start": v(-6537.5, -39) * mm, "end": v(-6677.5, -39) * mm});
            skLineSegment(sketch, "E166.1.0.1", {"start": v(-6537.5, -17) * mm, "end": v(-6677.5, -17) * mm});
            skLineSegment(sketch, "E166.1.0.2", {"start": v(-6537.5, -39) * mm, "end": v(-6537.5, -17) * mm});
            skLineSegment(sketch, "E166.1.0.3", {"start": v(-6677.5, -39) * mm, "end": v(-6677.5, -17) * mm});
            skLineSegment(sketch, "E166.2.0.0", {"start": v(-6775, -39) * mm, "end": v(-6915, -39) * mm});
            skLineSegment(sketch, "E166.2.0.1", {"start": v(-6775, -17) * mm, "end": v(-6915, -17) * mm});
            skLineSegment(sketch, "E166.2.0.2", {"start": v(-6775, -39) * mm, "end": v(-6775, -17) * mm});
            skLineSegment(sketch, "E166.2.0.3", {"start": v(-6915, -39) * mm, "end": v(-6915, -17) * mm});
            skLineSegment(sketch, "E166.3.0.0", {"start": v(-7012.5, -39) * mm, "end": v(-7152.5, -39) * mm});
            skLineSegment(sketch, "E166.3.0.1", {"start": v(-7012.5, -17) * mm, "end": v(-7152.5, -17) * mm});
            skLineSegment(sketch, "E166.3.0.2", {"start": v(-7012.5, -39) * mm, "end": v(-7012.5, -17) * mm});
            skLineSegment(sketch, "E166.3.0.3", {"start": v(-7152.5, -39) * mm, "end": v(-7152.5, -17) * mm});
            skLineSegment(sketch, "E166.4.0.0", {"start": v(-7250, -39) * mm, "end": v(-7390, -39) * mm});
            skLineSegment(sketch, "E166.4.0.1", {"start": v(-7250, -17) * mm, "end": v(-7390, -17) * mm});
            skLineSegment(sketch, "E166.4.0.2", {"start": v(-7250, -39) * mm, "end": v(-7250, -17) * mm});
            skLineSegment(sketch, "E166.4.0.3", {"start": v(-7390, -39) * mm, "end": v(-7390, -17) * mm});
            skLineSegment(sketch, "E166.5.0.0", {"start": v(-7487.5, -39) * mm, "end": v(-7627.5, -39) * mm});
            skLineSegment(sketch, "E166.5.0.1", {"start": v(-7487.5, -17) * mm, "end": v(-7627.5, -17) * mm});
            skLineSegment(sketch, "E166.5.0.2", {"start": v(-7487.5, -39) * mm, "end": v(-7487.5, -17) * mm});
            skLineSegment(sketch, "E166.5.0.3", {"start": v(-7627.5, -39) * mm, "end": v(-7627.5, -17) * mm});
            skLineSegment(sketch, "E166.6.0.0", {"start": v(-7725, -39) * mm, "end": v(-7865, -39) * mm});
            skLineSegment(sketch, "E166.6.0.1", {"start": v(-7725, -17) * mm, "end": v(-7865, -17) * mm});
            skLineSegment(sketch, "E166.6.0.2", {"start": v(-7725, -39) * mm, "end": v(-7725, -17) * mm});
            skLineSegment(sketch, "E166.6.0.3", {"start": v(-7865, -39) * mm, "end": v(-7865, -17) * mm});
            skLineSegment(sketch, "E166.7.0.0", {"start": v(-7962.5, -39) * mm, "end": v(-8102.5, -39) * mm});
            skLineSegment(sketch, "E166.7.0.1", {"start": v(-7962.5, -17) * mm, "end": v(-8102.5, -17) * mm});
            skLineSegment(sketch, "E166.7.0.2", {"start": v(-7962.5, -39) * mm, "end": v(-7962.5, -17) * mm});
            skLineSegment(sketch, "E166.7.0.3", {"start": v(-8102.5, -39) * mm, "end": v(-8102.5, -17) * mm});
            skLineSegment(sketch, "E166.8.0.0", {"start": v(-8200, -39) * mm, "end": v(-8340, -39) * mm});
            skLineSegment(sketch, "E166.8.0.1", {"start": v(-8200, -17) * mm, "end": v(-8340, -17) * mm});
            skLineSegment(sketch, "E166.8.0.2", {"start": v(-8200, -39) * mm, "end": v(-8200, -17) * mm});
            skLineSegment(sketch, "E166.8.0.3", {"start": v(-8340, -39) * mm, "end": v(-8340, -17) * mm});
            skLineSegment(sketch, "E166.direction1", {"start": v(-6440, -39) * mm, "end": v(-6677.5, -39) * mm, "construction": true});
            skLineSegment(sketch, "E167", {"start": v(-6488.75, -17) * mm, "end": v(-6488.75, -53.53) * mm, "construction": true});
            skLineSegment(sketch, "E168.bottom", {"start": v(-6418.75, -61) * mm, "end": v(-6558.75, -61) * mm});
            skLineSegment(sketch, "E168.top", {"start": v(-6418.75, -83) * mm, "end": v(-6558.75, -83) * mm});
            skLineSegment(sketch, "E168.left", {"start": v(-6418.75, -61) * mm, "end": v(-6418.75, -83) * mm});
            skLineSegment(sketch, "E168.right", {"start": v(-6558.75, -61) * mm, "end": v(-6558.75, -83) * mm});
            skLineSegment(sketch, "E169.1.0.0", {"start": v(-6656.25, -83) * mm, "end": v(-6796.25, -83) * mm});
            skLineSegment(sketch, "E169.1.0.1", {"start": v(-6656.25, -61) * mm, "end": v(-6796.25, -61) * mm});
            skLineSegment(sketch, "E169.1.0.2", {"start": v(-6796.25, -61) * mm, "end": v(-6796.25, -83) * mm});
            skLineSegment(sketch, "E169.1.0.3", {"start": v(-6656.25, -61) * mm, "end": v(-6656.25, -83) * mm});
            skLineSegment(sketch, "E169.2.0.0", {"start": v(-6893.75, -83) * mm, "end": v(-7033.75, -83) * mm});
            skLineSegment(sketch, "E169.2.0.1", {"start": v(-6893.75, -61) * mm, "end": v(-7033.75, -61) * mm});
            skLineSegment(sketch, "E169.2.0.2", {"start": v(-7033.75, -61) * mm, "end": v(-7033.75, -83) * mm});
            skLineSegment(sketch, "E169.2.0.3", {"start": v(-6893.75, -61) * mm, "end": v(-6893.75, -83) * mm});
            skLineSegment(sketch, "E169.3.0.0", {"start": v(-7131.25, -83) * mm, "end": v(-7271.25, -83) * mm});
            skLineSegment(sketch, "E169.3.0.1", {"start": v(-7131.25, -61) * mm, "end": v(-7271.25, -61) * mm});
            skLineSegment(sketch, "E169.3.0.2", {"start": v(-7271.25, -61) * mm, "end": v(-7271.25, -83) * mm});
            skLineSegment(sketch, "E169.3.0.3", {"start": v(-7131.25, -61) * mm, "end": v(-7131.25, -83) * mm});
            skLineSegment(sketch, "E169.4.0.0", {"start": v(-7368.75, -83) * mm, "end": v(-7508.75, -83) * mm});
            skLineSegment(sketch, "E169.4.0.1", {"start": v(-7368.75, -61) * mm, "end": v(-7508.75, -61) * mm});
            skLineSegment(sketch, "E169.4.0.2", {"start": v(-7508.75, -61) * mm, "end": v(-7508.75, -83) * mm});
            skLineSegment(sketch, "E169.4.0.3", {"start": v(-7368.75, -61) * mm, "end": v(-7368.75, -83) * mm});
            skLineSegment(sketch, "E169.5.0.0", {"start": v(-7606.25, -83) * mm, "end": v(-7746.25, -83) * mm});
            skLineSegment(sketch, "E169.5.0.1", {"start": v(-7606.25, -61) * mm, "end": v(-7746.25, -61) * mm});
            skLineSegment(sketch, "E169.5.0.2", {"start": v(-7746.25, -61) * mm, "end": v(-7746.25, -83) * mm});
            skLineSegment(sketch, "E169.5.0.3", {"start": v(-7606.25, -61) * mm, "end": v(-7606.25, -83) * mm});
            skLineSegment(sketch, "E169.6.0.0", {"start": v(-7843.75, -83) * mm, "end": v(-7983.75, -83) * mm});
            skLineSegment(sketch, "E169.6.0.1", {"start": v(-7843.75, -61) * mm, "end": v(-7983.75, -61) * mm});
            skLineSegment(sketch, "E169.6.0.2", {"start": v(-7983.75, -61) * mm, "end": v(-7983.75, -83) * mm});
            skLineSegment(sketch, "E169.6.0.3", {"start": v(-7843.75, -61) * mm, "end": v(-7843.75, -83) * mm});
            skLineSegment(sketch, "E169.7.0.0", {"start": v(-8081.25, -83) * mm, "end": v(-8221.25, -83) * mm});
            skLineSegment(sketch, "E169.7.0.1", {"start": v(-8081.25, -61) * mm, "end": v(-8221.25, -61) * mm});
            skLineSegment(sketch, "E169.7.0.2", {"start": v(-8221.25, -61) * mm, "end": v(-8221.25, -83) * mm});
            skLineSegment(sketch, "E169.7.0.3", {"start": v(-8081.25, -61) * mm, "end": v(-8081.25, -83) * mm});
            skLineSegment(sketch, "E169.direction1", {"start": v(-6558.75, -83) * mm, "end": v(-6796.25, -83) * mm, "construction": true});
            skLineSegment(sketch, "E170", {"start": v(-8390, -100) * mm, "end": v(-8390, -256) * mm, "construction": true});
            skLineSegment(sketch, "E171.MirrorCS", {"start": v(-10340, -39) * mm, "end": v(-10340, -17) * mm});
            skLineSegment(sketch, "E172.MirrorCS", {"start": v(-10102.5, -39) * mm, "end": v(-10102.5, -17) * mm});
            skLineSegment(sketch, "E173.MirrorCS", {"start": v(-9983.75, -61) * mm, "end": v(-9983.75, -83) * mm});
            skLineSegment(sketch, "E174.MirrorCS", {"start": v(-10221.25, -61) * mm, "end": v(-10221.25, -83) * mm});
            skLineSegment(sketch, "E175.MirrorCS", {"start": v(-10361.25, -61) * mm, "end": v(-10361.25, -83) * mm});
            skLineSegment(sketch, "E176.MirrorCS", {"start": v(-8558.75, -61) * mm, "end": v(-8558.75, -83) * mm});
            skLineSegment(sketch, "E177.MirrorCS", {"start": v(-9508.75, -61) * mm, "end": v(-9508.75, -83) * mm});
            skLineSegment(sketch, "E178.MirrorCS", {"start": v(-10005, -39) * mm, "end": v(-10005, -17) * mm});
            skLineSegment(sketch, "E179.MirrorCS", {"start": v(-9865, -39) * mm, "end": v(-9865, -17) * mm});
            skLineSegment(sketch, "E180.MirrorCS", {"start": v(-8817.5, -39) * mm, "end": v(-8817.5, -17) * mm});
            skLineSegment(sketch, "E181.MirrorCS", {"start": v(-10480, -39) * mm, "end": v(-10480, -17) * mm});
            skLineSegment(sketch, "E182.MirrorCS", {"start": v(-9767.5, -39) * mm, "end": v(-9767.5, -17) * mm});
            skLineSegment(sketch, "E183.MirrorCS", {"start": v(-10242.5, -39) * mm, "end": v(-10242.5, -17) * mm});
            skLineSegment(sketch, "E184.MirrorCS", {"start": v(-8698.75, -61) * mm, "end": v(-8698.75, -83) * mm});
            skLineSegment(sketch, "E185.MirrorCS", {"start": v(-9648.75, -61) * mm, "end": v(-9648.75, -83) * mm});
            skLineSegment(sketch, "E186.MirrorCS", {"start": v(-9292.5, -39) * mm, "end": v(-9292.5, -17) * mm});
            skLineSegment(sketch, "E187.MirrorCS", {"start": v(-9033.75, -61) * mm, "end": v(-9033.75, -83) * mm});
            skLineSegment(sketch, "E188.MirrorCS", {"start": v(-8677.5, -39) * mm, "end": v(-8677.5, -17) * mm});
            skLineSegment(sketch, "E189.MirrorCS", {"start": v(-9627.5, -39) * mm, "end": v(-9627.5, -17) * mm});
            skLineSegment(sketch, "E190.MirrorCS", {"start": v(-9152.5, -39) * mm, "end": v(-9152.5, -17) * mm});
            skLineSegment(sketch, "E191.MirrorCS", {"start": v(-9746.25, -61) * mm, "end": v(-9746.25, -83) * mm});
            skLineSegment(sketch, "E192.MirrorCS", {"start": v(-8796.25, -61) * mm, "end": v(-8796.25, -83) * mm});
            skLineSegment(sketch, "E193.MirrorCS", {"start": v(-9411.25, -61) * mm, "end": v(-9411.25, -83) * mm});
            skLineSegment(sketch, "E194.MirrorCS", {"start": v(-9271.25, -61) * mm, "end": v(-9271.25, -83) * mm});
            skLineSegment(sketch, "E195.MirrorCS", {"start": v(-9886.25, -61) * mm, "end": v(-9886.25, -83) * mm});
            skLineSegment(sketch, "E196.MirrorCS", {"start": v(-9055, -39) * mm, "end": v(-9055, -17) * mm});
            skLineSegment(sketch, "E197.MirrorCS", {"start": v(-8915, -39) * mm, "end": v(-8915, -17) * mm});
            skLineSegment(sketch, "E198.MirrorCS", {"start": v(-8580, -39) * mm, "end": v(-8580, -17) * mm});
            skLineSegment(sketch, "E199.MirrorCS", {"start": v(-9530, -39) * mm, "end": v(-9530, -17) * mm});
            skLineSegment(sketch, "E200.MirrorCS", {"start": v(-9173.75, -61) * mm, "end": v(-9173.75, -83) * mm});
            skLineSegment(sketch, "E201.MirrorCS", {"start": v(-10123.75, -61) * mm, "end": v(-10123.75, -83) * mm});
            skLineSegment(sketch, "E202.MirrorCS", {"start": v(-8440, -39) * mm, "end": v(-8440, -17) * mm});
            skLineSegment(sketch, "E203.MirrorCS", {"start": v(-9390, -39) * mm, "end": v(-9390, -17) * mm});
            skLineSegment(sketch, "E204.MirrorCS", {"start": v(-8936.25, -61) * mm, "end": v(-8936.25, -83) * mm});
            skLineSegment(sketch, "E205.MirrorCS", {"start": v(-10242.5, -39) * mm, "end": v(-10102.5, -39) * mm});
            skLineSegment(sketch, "E206.MirrorCS", {"start": v(-10291.25, -17) * mm, "end": v(-10291.25, -53.53) * mm, "construction": true});
            skLineSegment(sketch, "E207.MirrorCS", {"start": v(-10123.75, -83) * mm, "end": v(-9983.75, -83) * mm});
            skLineSegment(sketch, "E208.MirrorCS", {"start": v(-9292.5, -39) * mm, "end": v(-9152.5, -39) * mm});
            skLineSegment(sketch, "E209.MirrorCS", {"start": v(-10005, -17) * mm, "end": v(-9865, -17) * mm});
            skLineSegment(sketch, "E210.MirrorCS", {"start": v(-10340, -39) * mm, "end": v(-10102.5, -39) * mm, "construction": true});
            skLineSegment(sketch, "E211.MirrorCS", {"start": v(-10480, -39) * mm, "end": v(-10340, -39) * mm});
            skLineSegment(sketch, "E212.MirrorCS", {"start": v(-10480, -17) * mm, "end": v(-10340, -17) * mm});
            skLineSegment(sketch, "E213.MirrorCS", {"start": v(-9886.25, -83) * mm, "end": v(-9746.25, -83) * mm});
            skLineSegment(sketch, "E214.MirrorCS", {"start": v(-8936.25, -83) * mm, "end": v(-8796.25, -83) * mm});
            skLineSegment(sketch, "E215.MirrorCS", {"start": v(-9292.5, -17) * mm, "end": v(-9152.5, -17) * mm});
            skLineSegment(sketch, "E216.MirrorCS", {"start": v(-10242.5, -17) * mm, "end": v(-10102.5, -17) * mm});
            skLineSegment(sketch, "E217.MirrorCS", {"start": v(-10005, -39) * mm, "end": v(-9865, -39) * mm});
            skLineSegment(sketch, "E218.MirrorCS", {"start": v(-8936.25, -61) * mm, "end": v(-8796.25, -61) * mm});
            skLineSegment(sketch, "E219.MirrorCS", {"start": v(-10221.25, -83) * mm, "end": v(-9983.75, -83) * mm, "construction": true});
            skLineSegment(sketch, "E220.MirrorCS", {"start": v(-9411.25, -83) * mm, "end": v(-9271.25, -83) * mm});
            skLineSegment(sketch, "E221.MirrorCS", {"start": v(-10361.25, -61) * mm, "end": v(-10221.25, -61) * mm});
            skLineSegment(sketch, "E222.MirrorCS", {"start": v(-9767.5, -39) * mm, "end": v(-9627.5, -39) * mm});
            skLineSegment(sketch, "E223.MirrorCS", {"start": v(-8817.5, -39) * mm, "end": v(-8677.5, -39) * mm});
            skLineSegment(sketch, "E224.MirrorCS", {"start": v(-9886.25, -61) * mm, "end": v(-9746.25, -61) * mm});
            skLineSegment(sketch, "E225.MirrorCS", {"start": v(-9411.25, -61) * mm, "end": v(-9271.25, -61) * mm});
            skLineSegment(sketch, "E226.MirrorCS", {"start": v(-10361.25, -83) * mm, "end": v(-10221.25, -83) * mm});
            skLineSegment(sketch, "E227.MirrorCS", {"start": v(-8580, -39) * mm, "end": v(-8440, -39) * mm});
            skLineSegment(sketch, "E228.MirrorCS", {"start": v(-9055, -17) * mm, "end": v(-8915, -17) * mm});
            skLineSegment(sketch, "E229.MirrorCS", {"start": v(-9530, -39) * mm, "end": v(-9390, -39) * mm});
            skLineSegment(sketch, "E230.MirrorCS", {"start": v(-9055, -39) * mm, "end": v(-8915, -39) * mm});
            skLineSegment(sketch, "E231.MirrorCS", {"start": v(-8580, -17) * mm, "end": v(-8440, -17) * mm});
            skLineSegment(sketch, "E232.MirrorCS", {"start": v(-9530, -17) * mm, "end": v(-9390, -17) * mm});
            skLineSegment(sketch, "E233.MirrorCS", {"start": v(-10123.75, -61) * mm, "end": v(-9983.75, -61) * mm});
            skLineSegment(sketch, "E234.MirrorCS", {"start": v(-9648.75, -83) * mm, "end": v(-9508.75, -83) * mm});
            skLineSegment(sketch, "E235.MirrorCS", {"start": v(-8698.75, -83) * mm, "end": v(-8558.75, -83) * mm});
            skLineSegment(sketch, "E236.MirrorCS", {"start": v(-9767.5, -17) * mm, "end": v(-9627.5, -17) * mm});
            skLineSegment(sketch, "E237.MirrorCS", {"start": v(-9173.75, -61) * mm, "end": v(-9033.75, -61) * mm});
            skLineSegment(sketch, "E238.MirrorCS", {"start": v(-8817.5, -17) * mm, "end": v(-8677.5, -17) * mm});
            skLineSegment(sketch, "E239.MirrorCS", {"start": v(-9648.75, -61) * mm, "end": v(-9508.75, -61) * mm});
            skLineSegment(sketch, "E240.MirrorCS", {"start": v(-8698.75, -61) * mm, "end": v(-8558.75, -61) * mm});
            skLineSegment(sketch, "E241.MirrorCS", {"start": v(-9173.75, -83) * mm, "end": v(-9033.75, -83) * mm});
            skSolve(sketch);
        }
        {
            var Q0;
            Q0 = qSketchRegion(id + "F10", true);
            extrude(context, id + "F11", {"entities" : qUnion([Q0]), "oppositeDirection" : true, "depth" : 1900 * mm, "hasSecondDirection" : true, "secondDirectionOppositeDirection" : true, "secondDirectionDepth" : 100 * mm});
        }
        {
            var Q0;
            Q0=makeQuery(id+"F3.opExtrude","SWEPT_FACE",FACE,{"disambiguationData":[OSD([sQuery(id+"F0.wireOp",EDGE,"E5.right")])]});
            var sketch = newSketch(context, id + "F12", { "sketchPlane" : qUnion([Q0])});
            skLineSegment(sketch, "E242.bottom", {"start": v(-61, -240) * mm, "end": v(-39, -240) * mm});
            skLineSegment(sketch, "E242.top", {"start": v(-61, -170) * mm, "end": v(-39, -170) * mm});
            skLineSegment(sketch, "E242.left", {"start": v(-61, -240) * mm, "end": v(-61, -170) * mm});
            skLineSegment(sketch, "E242.right", {"start": v(-39, -240) * mm, "end": v(-39, -170) * mm});
            skLineSegment(sketch, "E243.bottom", {"start": v(-61, 1190) * mm, "end": v(-39, 1190) * mm});
            skLineSegment(sketch, "E243.top", {"start": v(-61, 1260) * mm, "end": v(-39, 1260) * mm});
            skLineSegment(sketch, "E243.left", {"start": v(-61, 1190) * mm, "end": v(-61, 1260) * mm});
            skLineSegment(sketch, "E243.right", {"start": v(-39, 1190) * mm, "end": v(-39, 1260) * mm});
            skSolve(sketch);
        }
        {
            var Q0;
            Q0 = qSketchRegion(id + "F12", true);
            var Q1;
            Q1=makeQuery(id+"F2.opExtrude","SWEPT_FACE",FACE,{"disambiguationData":[OSD([sQuery(id+"F0.wireOp",EDGE,"E2.right")])]});
            extrude(context, id + "F13", {"entities" : qUnion([Q0]), "endBound" : BoundingType.UP_TO_SURFACE, "oppositeDirection" : true, "endBoundEntityFace" : qUnion([Q1]), "depth" : 25 * mm, "hasSecondDirection" : true, "secondDirectionOppositeDirection" : true, "secondDirectionDepth" : 10 * mm});
        }
    });
